FCSTD DOCUMENT  (FreeCAD 0.20R29410 (Git))
Label: kv-03
License: All rights reserved
LicenseURL: http://en.wikipedia.org/wiki/All_rights_reserved
objects: Sketcher::SketchObject×1, PartDesign::Body×1
note: 2 computed .brp shape members not serialized (recipe doc carries the construction recipe); baked Part::Feature solids carry a one-line shape summary decoded from their .brp

FEATURE [Sketcher::SketchObject] Sketch
  FullyConstrained = false
  MapMode = 5
  Placement = pos=(0,0,0) rot=(1,0,0;1.5708rad)
  Support = -> [XZ_Plane]
  sketch-geometry (4):
    g0: LineSegment StartX=0 StartY=0 StartZ=0 EndX=50.8283 EndY=0 EndZ=0
    g1: LineSegment StartX=50.8283 StartY=0 StartZ=0 EndX=50.8283 EndY=49.6111 EndZ=0
    g2: LineSegment StartX=50.8283 StartY=49.6111 StartZ=0 EndX=0 EndY=49.6111 EndZ=0
    g3: LineSegment StartX=0 StartY=49.6111 StartZ=0 EndX=0 EndY=0 EndZ=0
  constraints (9):
    c: Coincident(g0,g1)
    c: Coincident(g1,g2)
    c: Coincident(g2,g3)
    c: Coincident(g3,g0)
    c: Horizontal(g0)
    c: Horizontal(g2)
    c: Vertical(g1)
    c: Vertical(g3)
    c: Coincident(g0,g-1)
FEATURE [PartDesign::Body] Body
  Group = -> [Sketch]
  Origin = -> Origin
